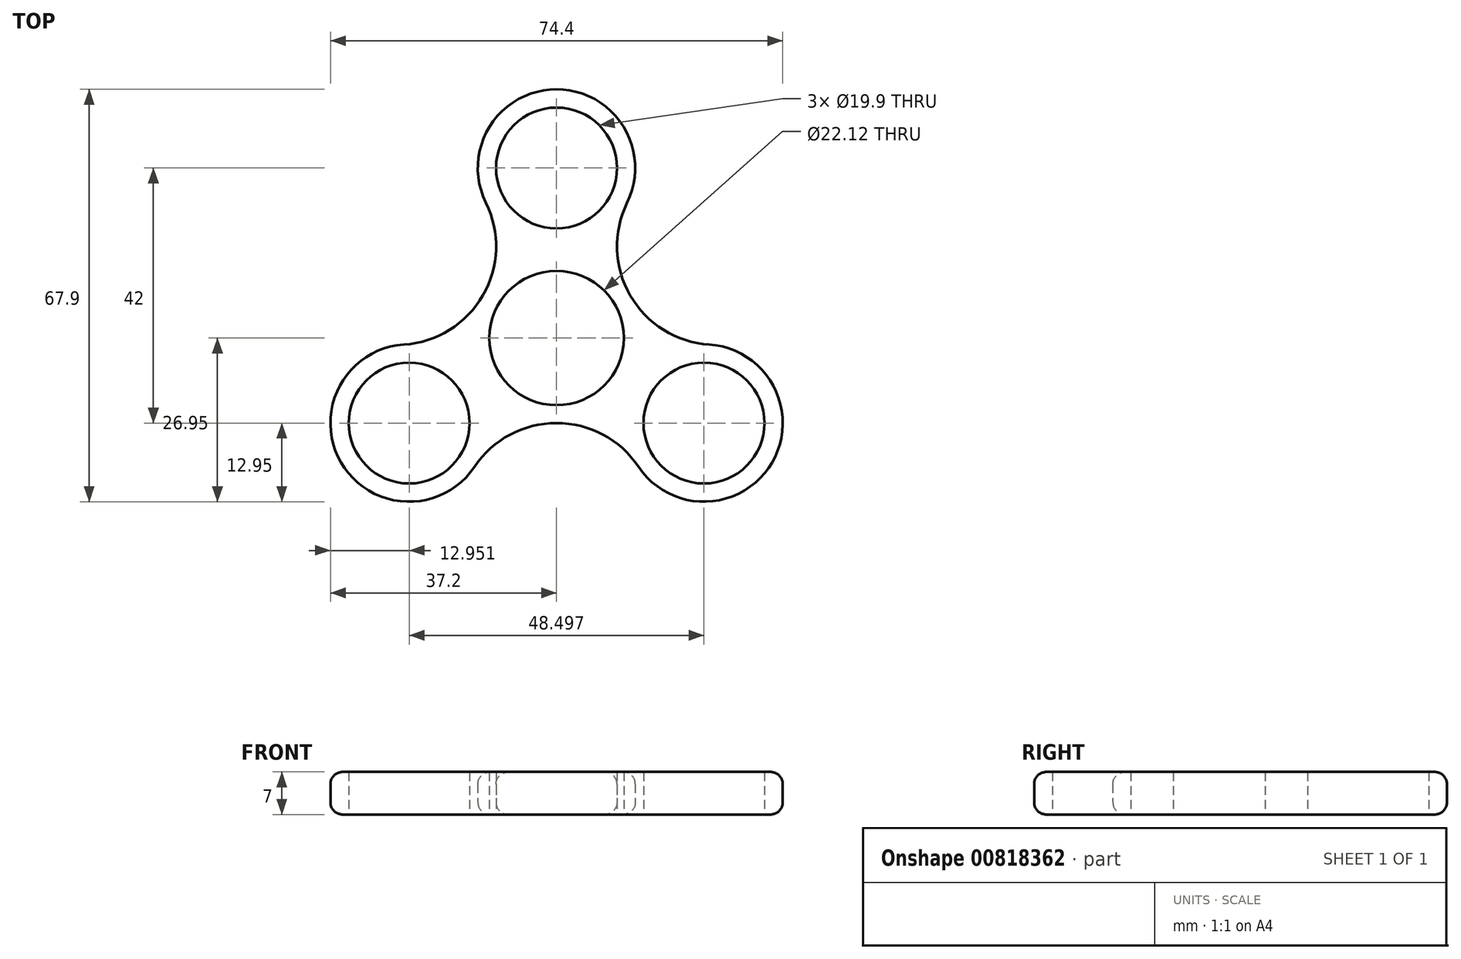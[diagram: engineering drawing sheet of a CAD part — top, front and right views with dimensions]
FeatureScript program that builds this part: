
annotation { "Feature Type Name" : "Feature", "Feature Type Description" : "" }
export const myFeature = defineFeature(function(context is Context, id is Id, definition is map)
    precondition{}
    {
        {
            var Q0;
            Q0=qCreatedBy(makeId("Top.planeOp"),FACE);
            var sketch = newSketch(context, id + "F0", { "sketchPlane" : qUnion([Q0])});
            skCircle(sketch, "E0", {"center": v(0, 0) * mm, "radius": 11.06 * mm});
            skCircle(sketch, "E1", {"center": v(0, 28) * mm, "radius": 9.95 * mm});
            skArc(sketch, "E2.0", {"start": v(11.62, 22.28) * mm, "mid": v(0, 40.95) * mm, "end": v(-11.62, 22.28) * mm});
            skCircle(sketch, "E3.1.0", {"center": v(-24.25, -14) * mm, "radius": 9.95 * mm});
            skArc(sketch, "E3.1.1", {"start": v(-25.1, -1.08) * mm, "mid": v(-35.46, -20.47) * mm, "end": v(-13.49, -21.2) * mm});
            skCircle(sketch, "E3.2.0", {"center": v(24.25, -14) * mm, "radius": 9.95 * mm});
            skArc(sketch, "E3.2.1", {"start": v(13.49, -21.2) * mm, "mid": v(35.46, -20.48) * mm, "end": v(25.1, -1.08) * mm});
            skLineSegment(sketch, "E4", {"start": v(-24.25, -14) * mm, "end": v(50.87, 29.37) * mm, "construction": true});
            skLineSegment(sketch, "E5", {"start": v(24.25, -14) * mm, "end": v(0, 28) * mm, "construction": true});
            skArc(sketch, "E6", {"start": v(11.62, 22.28) * mm, "mid": v(12.12, 7) * mm, "end": v(25.1, -1.08) * mm});
            skArc(sketch, "E7.1.0", {"start": v(-25.1, -1.08) * mm, "mid": v(-12.12, 7) * mm, "end": v(-11.62, 22.28) * mm});
            skArc(sketch, "E7.2.0", {"start": v(13.49, -21.2) * mm, "mid": v(0, -14) * mm, "end": v(-13.49, -21.2) * mm});
            skLineSegment(sketch, "E8", {"start": v(0, 0) * mm, "end": v(24.25, -14) * mm, "construction": true});
            skSolve(sketch);
        }
        {
            var Q0;
            Q0=makeQuery(id+"F0.imprint","IMPRINT",FACE,{"disambiguationData":[TD([[makeQuery(id+"F0.imprint","IMPRINT",EDGE,{"derivedFrom":sQuery(id+"F0.wireOp",EDGE,"E0")}),-1.0]])]});
            extrude(context, id + "F1", {"entities" : qUnion([Q0]), "depth" : 7 * mm, "offsetDistance" : 25 * mm});
        }
        {
            var Q0;
            Q0=makeQuery(id+"F1.opExtrude","CAP_EDGE",EDGE,{"disambiguationData":[OSD([sQuery(id+"F0.wireOp",EDGE,"E7.2.0")])],"isStart":false});
            var Q1;
            Q1=makeQuery(id+"F1.opExtrude","CAP_EDGE",EDGE,{"disambiguationData":[OSD([sQuery(id+"F0.wireOp",EDGE,"E7.2.0")])],"isStart":true});
            fillet(context, id + "F2", {"entities" : qUnion([Q0, Q1]), "radius" : 2 * mm, "tangentPropagation" : true, "allowEdgeOverflow" : false});
        }
    });
